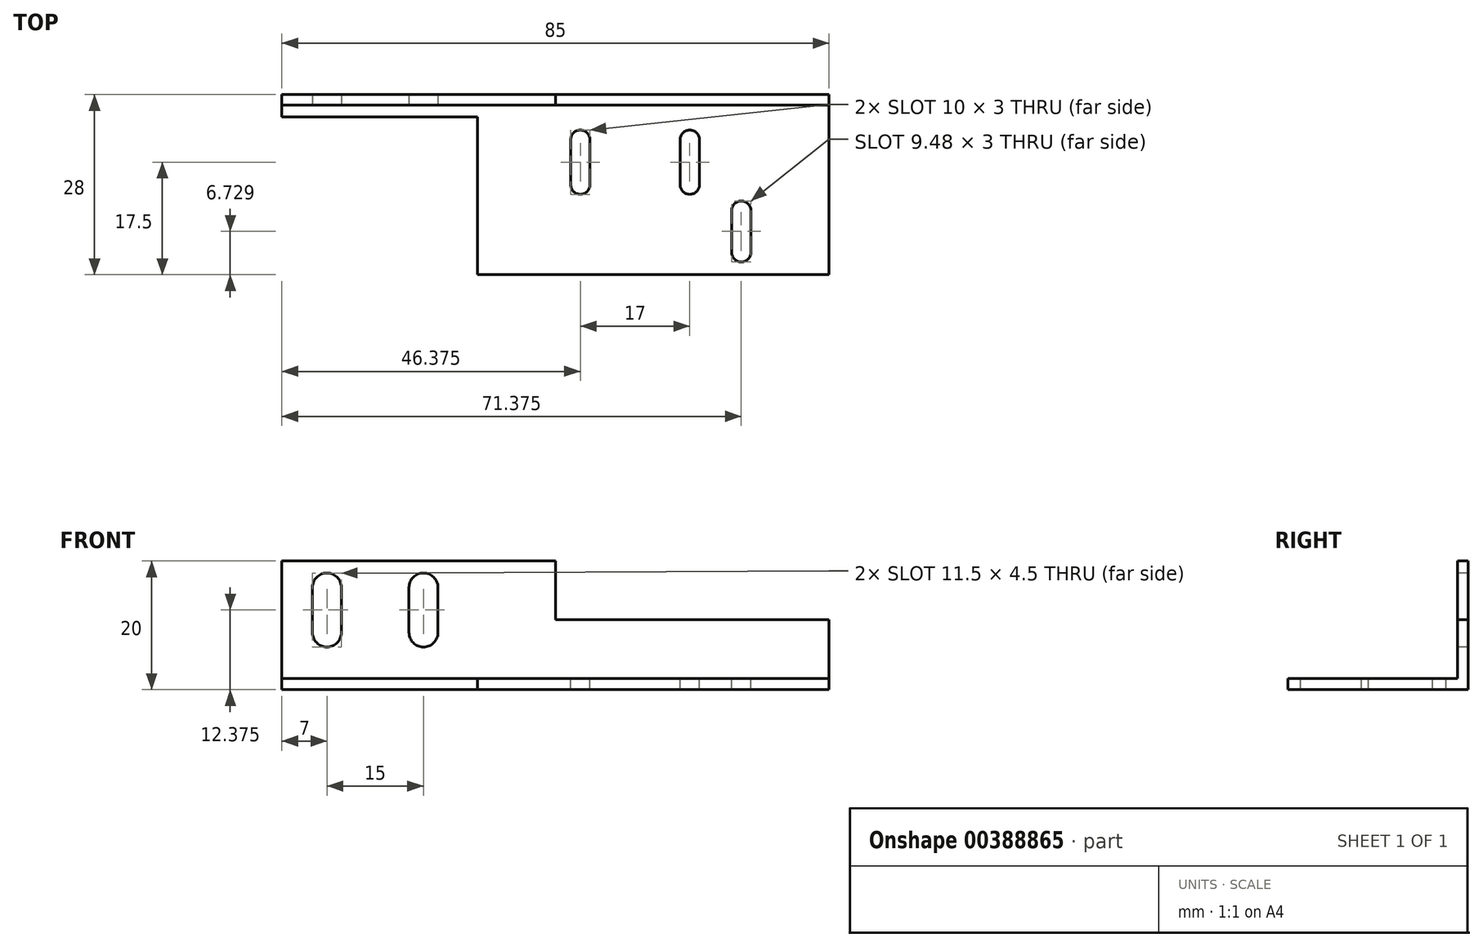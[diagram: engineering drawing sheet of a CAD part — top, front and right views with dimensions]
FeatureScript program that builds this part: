
annotation { "Feature Type Name" : "Feature", "Feature Type Description" : "" }
export const myFeature = defineFeature(function(context is Context, id is Id, definition is map)
    precondition{}
    {
        {
            var Q0;
            Q0=qCreatedBy(makeId("Top.planeOp"),FACE);
            var sketch = newSketch(context, id + "F0", { "sketchPlane" : qUnion([Q0])});
            skLineSegment(sketch, "E0.bottom", {"start": v(42.5, -14) * mm, "end": v(-42.5, -14) * mm});
            skLineSegment(sketch, "E0.top", {"start": v(42.5, 14) * mm, "end": v(-42.5, 14) * mm});
            skLineSegment(sketch, "E0.left", {"start": v(42.5, -14) * mm, "end": v(42.5, 14) * mm});
            skLineSegment(sketch, "E0.right", {"start": v(-42.5, -14) * mm, "end": v(-42.5, 14) * mm});
            skPoint(sketch, "E0.middle", {"position": v(0, 0) * mm});
            skSolve(sketch);
        }
        {
            var Q0;
            Q0 = qSketchRegion(id + "F0", true);
            extrude(context, id + "F1", {"entities" : qUnion([Q0]), "depth" : 20 * mm, "offsetDistance" : 25 * mm});
        }
        {
            var Q0;
            Q0=makeQuery(id+"F1.opExtrude","SWEPT_FACE",FACE,{"disambiguationData":[OSD([sQuery(id+"F0.wireOp",EDGE,"E0.left")])]});
            var sketch = newSketch(context, id + "F2", { "sketchPlane" : qUnion([Q0])});
            skLineSegment(sketch, "E1", {"start": v(12.37, 20) * mm, "end": v(12.37, 1.75) * mm});
            skLineSegment(sketch, "E2", {"start": v(12.37, 1.75) * mm, "end": v(-14, 1.75) * mm});
            skLineSegment(sketch, "E3", {"start": v(-14, 1.75) * mm, "end": v(-14, 20) * mm});
            skLineSegment(sketch, "E4", {"start": v(-14, 20) * mm, "end": v(12.37, 20) * mm});
            skSolve(sketch);
        }
        {
            var Q0;
            Q0 = qSketchRegion(id + "F2", true);
            extrude(context, id + "F3", {"entities" : qUnion([Q0]), "operationType" : NewBodyOperationType.REMOVE, "oppositeDirection" : true, "depth" : 121 * mm, "offsetDistance" : 25 * mm});
        }
        {
            var Q0;
            Q0=makeQuery(id+"F3.boolean.opBoolean","COPY",FACE,{"derivedFrom":makeQuery(id+"F3.opExtrude","SWEPT_FACE",FACE,{"disambiguationData":[OSD([sQuery(id+"F2.wireOp",EDGE,"E2")])]})});
            var sketch = newSketch(context, id + "F4", { "sketchPlane" : qUnion([Q0])});
            skLineSegment(sketch, "E5", {"start": v(-42.5, -14) * mm, "end": v(-12.12, -14) * mm});
            skLineSegment(sketch, "E6", {"start": v(-12.12, -14) * mm, "end": v(-12.12, 10.56) * mm});
            skLineSegment(sketch, "E7", {"start": v(-12.12, 10.56) * mm, "end": v(-42.5, 10.56) * mm});
            skLineSegment(sketch, "E8", {"start": v(-42.5, 10.56) * mm, "end": v(-42.5, -14) * mm});
            skSolve(sketch);
        }
        {
            var Q0;
            Q0 = qSketchRegion(id + "F4", true);
            extrude(context, id + "F5", {"entities" : qUnion([Q0]), "operationType" : NewBodyOperationType.REMOVE, "oppositeDirection" : true, "depth" : 25 * mm, "offsetDistance" : 25 * mm});
        }
        {
            var Q0;
            Q0=makeQuery(id+"F3.boolean.opBoolean","COPY",FACE,{"derivedFrom":makeQuery(id+"F3.opExtrude","SWEPT_FACE",FACE,{"disambiguationData":[OSD([sQuery(id+"F2.wireOp",EDGE,"E1")])]})});
            var sketch = newSketch(context, id + "F6", { "sketchPlane" : qUnion([Q0])});
            skLineSegment(sketch, "E9", {"start": v(42.5, 20) * mm, "end": v(42.5, 10.87) * mm});
            skLineSegment(sketch, "E10", {"start": v(42.5, 10.87) * mm, "end": v(0, 10.87) * mm});
            skLineSegment(sketch, "E11", {"start": v(0, 10.87) * mm, "end": v(0, 20) * mm});
            skLineSegment(sketch, "E12", {"start": v(0, 20) * mm, "end": v(42.5, 20) * mm});
            skSolve(sketch);
        }
        {
            var Q0;
            Q0 = qSketchRegion(id + "F6", true);
            extrude(context, id + "F7", {"entities" : qUnion([Q0]), "operationType" : NewBodyOperationType.REMOVE, "oppositeDirection" : true, "depth" : 25 * mm, "offsetDistance" : 25 * mm});
        }
        {
            var Q0;
            Q0=makeQuery(id+"F3.boolean.opBoolean","COPY",FACE,{"derivedFrom":makeQuery(id+"F3.opExtrude","SWEPT_FACE",FACE,{"disambiguationData":[OSD([sQuery(id+"F2.wireOp",EDGE,"E1")])]})});
            var sketch = newSketch(context, id + "F8", { "sketchPlane" : qUnion([Q0])});
            skLineSegment(sketch, "E13", {"start": v(-50.99, 10.87) * mm, "end": v(54.79, 10.87) * mm, "construction": true});
            skPoint(sketch, "E13.startSnap0", {"position": v(-42.5, 10.87) * mm});
            skLineSegment(sketch, "E14", {"start": v(-51.1, 15.87) * mm, "end": v(7.54, 15.87) * mm, "construction": true});
            skLineSegment(sketch, "E15", {"start": v(-48.54, 8.87) * mm, "end": v(7.54, 8.87) * mm, "construction": true});
            skCircle(sketch, "E16", {"center": v(-35.5, 15.87) * mm, "radius": 2.25 * mm});
            skCircle(sketch, "E17", {"center": v(-35.5, 8.87) * mm, "radius": 2.25 * mm});
            skCircle(sketch, "E18", {"center": v(-20.5, 8.87) * mm, "radius": 2.25 * mm});
            skCircle(sketch, "E19", {"center": v(-20.5, 15.87) * mm, "radius": 2.25 * mm});
            skPoint(sketch, "E19.centerSnap0", {"position": v(-21.78, 15.87) * mm});
            skLineSegment(sketch, "E20", {"start": v(-37.75, 15.87) * mm, "end": v(-37.75, 8.87) * mm});
            skLineSegment(sketch, "E21", {"start": v(-33.25, 8.87) * mm, "end": v(-33.25, 15.87) * mm});
            skLineSegment(sketch, "E22", {"start": v(-22.75, 15.87) * mm, "end": v(-22.75, 8.87) * mm});
            skLineSegment(sketch, "E23", {"start": v(-18.25, 8.87) * mm, "end": v(-18.25, 15.87) * mm});
            skSolve(sketch);
        }
        {
            var Q0;
            Q0 = qSketchRegion(id + "F8", true);
            extrude(context, id + "F9", {"entities" : qUnion([Q0]), "operationType" : NewBodyOperationType.REMOVE, "oppositeDirection" : true, "depth" : 25 * mm, "offsetDistance" : 25 * mm});
        }
        {
            var Q0;
            Q0=makeQuery(id+"F3.boolean.opBoolean","COPY",FACE,{"derivedFrom":makeQuery(id+"F3.opExtrude","SWEPT_FACE",FACE,{"disambiguationData":[OSD([sQuery(id+"F2.wireOp",EDGE,"E2")])]})});
            var sketch = newSketch(context, id + "F10", { "sketchPlane" : qUnion([Q0])});
            skLineSegment(sketch, "E24", {"start": v(31.67, 0) * mm, "end": v(-10.71, 0) * mm, "construction": true});
            skLineSegment(sketch, "E25", {"start": v(10.47, -11.8) * mm, "end": v(10.47, 13.36) * mm, "construction": true});
            skLineSegment(sketch, "E26", {"start": v(20.88, 13.36) * mm, "end": v(20.88, -11.46) * mm, "construction": true});
            skLineSegment(sketch, "E27", {"start": v(28.45, -11.94) * mm, "end": v(28.88, -11.46) * mm, "construction": true});
            skLineSegment(sketch, "E28", {"start": v(28.88, -11.46) * mm, "end": v(28.88, 13.36) * mm, "construction": true});
            skLineSegment(sketch, "E29", {"start": v(3.88, 13.36) * mm, "end": v(3.88, -11.46) * mm, "construction": true});
            skLineSegment(sketch, "E30", {"start": v(-10.26, 7) * mm, "end": v(30.86, 7) * mm, "construction": true});
            skLineSegment(sketch, "E31", {"start": v(-10.34, 0) * mm, "end": v(30.86, 0) * mm, "construction": true});
            skLineSegment(sketch, "E32", {"start": v(-10, -4.03) * mm, "end": v(31.67, -4.03) * mm, "construction": true});
            skLineSegment(sketch, "E33", {"start": v(31.67, -10.51) * mm, "end": v(-10, -10.51) * mm, "construction": true});
            skCircle(sketch, "E34", {"center": v(3.88, 7) * mm, "radius": 1.5 * mm});
            skCircle(sketch, "E35", {"center": v(20.88, 7) * mm, "radius": 1.5 * mm});
            skCircle(sketch, "E36", {"center": v(3.88, 0) * mm, "radius": 1.5 * mm});
            skCircle(sketch, "E37", {"center": v(20.88, 0) * mm, "radius": 1.5 * mm});
            skCircle(sketch, "E38", {"center": v(28.88, -4.03) * mm, "radius": 1.5 * mm});
            skCircle(sketch, "E39", {"center": v(28.88, -10.51) * mm, "radius": 1.5 * mm});
            skLineSegment(sketch, "E40", {"start": v(2.38, 7) * mm, "end": v(2.38, 0) * mm});
            skLineSegment(sketch, "E41", {"start": v(5.38, 7) * mm, "end": v(5.38, 0) * mm});
            skLineSegment(sketch, "E42", {"start": v(19.38, 7) * mm, "end": v(19.38, 0) * mm});
            skLineSegment(sketch, "E43", {"start": v(22.38, 7) * mm, "end": v(22.38, 0) * mm});
            skLineSegment(sketch, "E44", {"start": v(27.38, -4.03) * mm, "end": v(27.38, -10.51) * mm});
            skLineSegment(sketch, "E45", {"start": v(30.38, -4.03) * mm, "end": v(30.38, -10.51) * mm});
            skSolve(sketch);
        }
        {
            var Q0;
            Q0 = qSketchRegion(id + "F10", true);
            extrude(context, id + "F11", {"entities" : qUnion([Q0]), "operationType" : NewBodyOperationType.REMOVE, "oppositeDirection" : true, "depth" : 25 * mm, "offsetDistance" : 25 * mm});
        }
    });
